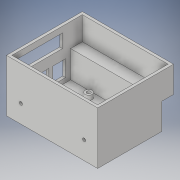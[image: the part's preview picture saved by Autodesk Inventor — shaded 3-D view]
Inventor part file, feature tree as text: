
AUTODESK INVENTOR PART (.ipt)
format: ipt  version: 2019.4 (Build 234330000, 330)  size: 219,648 bytes
history: native  units: mm
features: extrude x8, sketch x8
ambient origin geometry x8: Origin, YZ Plane, XZ Plane, XY Plane, X Axis, Y Axis, Z Axis, Center Point
bodies: Solid1 (feature_tree)
feature tree (16):
  extrude  "Extrusion1"  Depth=65.0mm
  extrude  "Extrusion2"  Depth=32.0mm TaperAngle=0.0deg
  extrude  "Extrusion3"  Depth=65.0mm
  extrude  "Extrusion4"  Depth=9.0mm
  extrude  "Extrusion5"  Depth=4.0mm
  extrude  "Extrusion6"  Depth=58.0mm
  extrude  "Extrusion7"  Depth=13.0mm
  extrude  "Extrusion8"  Depth=10.0mm
  sketch  "Sketch1"  dims[d0=95.0mm d1=65.0mm]
  sketch  "Sketch2"  dims[d2=3.0mm d3=32.0mm d4=0.0mm]
  sketch  "Sketch3"  dims[d5=95.0mm d6=65.0mm]
  sketch  "Sketch4"  dims[d7=30.0mm d8=0.0mm d9=9.0mm]
  sketch  "Sketch5"  dims[d10=10.0mm d11=4.0mm]
  sketch  "Sketch6"  dims[d12=8.0mm d13=20.0mm d15=49.0mm d16=20.0mm d18=58.0mm]
  sketch  "Sketch7"  dims[d21=5.0mm d22=0.0mm d23=13.0mm]
  sketch  "Sketch8"  dims[d24=3.0mm d25=0.0mm d26=100.0mm d27=3.0mm d28=3.0mm d29=84.0mm d30=3.0mm d31=84.0mm d32=100.0mm d33=3.0mm d34=26.0mm d35=0.0mm d36=9.142mm d37=6.5mm d38=50.0mm d39=15.0mm d40=5.0mm d41=90.0deg d42=5.54mm d43=14.0mm d44=18.0mm d45=4.5mm d46=14.0mm d47=18.0mm d48=3.0mm d49=0.0mm d50=1.0mm d51=5.0mm d52=27.75mm d53=8.0mm d54=4.0mm d55=3.0mm d56=0.0mm d62=101.0mm d63=20.0mm d64=15.0mm d65=70.0mm d66=3.5mm d67=3.5mm d68=10.0mm d69=0.0mm]
